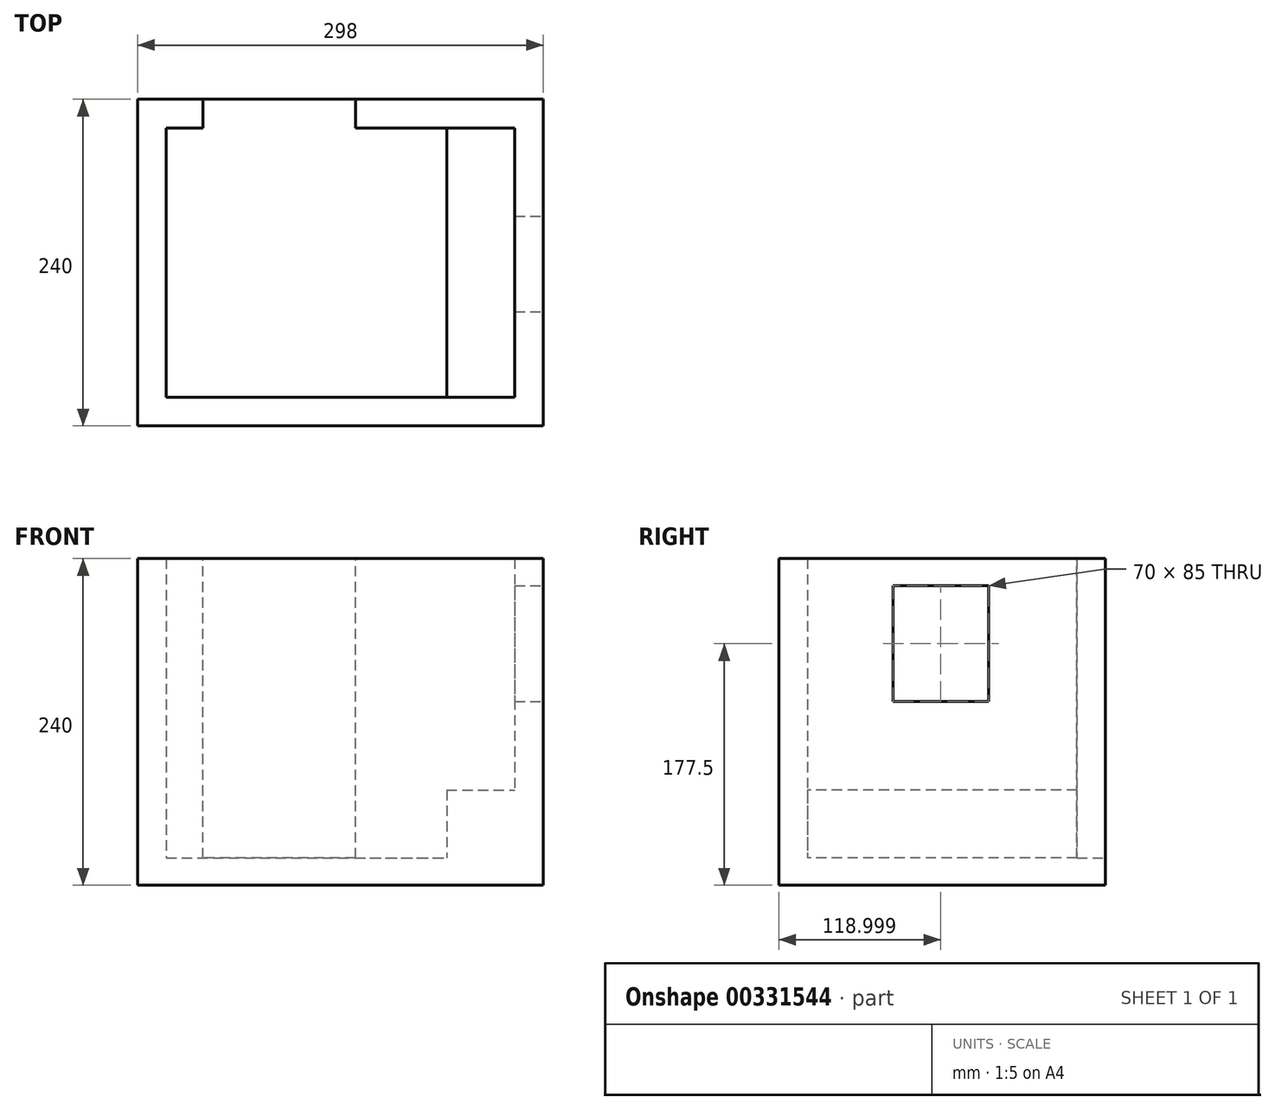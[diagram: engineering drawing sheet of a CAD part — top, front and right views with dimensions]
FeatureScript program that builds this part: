
annotation { "Feature Type Name" : "Feature", "Feature Type Description" : "" }
export const myFeature = defineFeature(function(context is Context, id is Id, definition is map)
    precondition{}
    {
        {
            var Q0;
            Q0=qCreatedBy(makeId("Top.planeOp"),FACE);
            var sketch = newSketch(context, id + "F0", { "sketchPlane" : qUnion([Q0])});
            skLineSegment(sketch, "E0", {"start": v(1313, 440) * mm, "end": v(1313, 406) * mm});
            skLineSegment(sketch, "E1", {"start": v(1313, -267) * mm, "end": v(1313, -301) * mm});
            skLineSegment(sketch, "E2", {"start": v(1313, -301) * mm, "end": v(647, -301) * mm});
            skLineSegment(sketch, "E3", {"start": v(1279, -267) * mm, "end": v(647, -267) * mm});
            skLineSegment(sketch, "E4", {"start": v(1279, 406) * mm, "end": v(688, 406) * mm});
            skLineSegment(sketch, "E5", {"start": v(688, 406) * mm, "end": v(688, -75) * mm});
            skLineSegment(sketch, "E6", {"start": v(688, -75) * mm, "end": v(413, -75) * mm});
            skLineSegment(sketch, "E7", {"start": v(647, -301) * mm, "end": v(647, -267) * mm});
            skLineSegment(sketch, "E8", {"start": v(536, -301) * mm, "end": v(536, -267) * mm});
            skLineSegment(sketch, "E9", {"start": v(536, -267) * mm, "end": v(328, -267) * mm});
            skLineSegment(sketch, "E10", {"start": v(328, -267) * mm, "end": v(328, -407) * mm});
            skLineSegment(sketch, "E11", {"start": v(328, -407) * mm, "end": v(-40, -407) * mm});
            skLineSegment(sketch, "E12", {"start": v(-40, -407) * mm, "end": v(-40, -188) * mm});
            skLineSegment(sketch, "E13", {"start": v(-40, -188) * mm, "end": v(-105, -188) * mm});
            skLineSegment(sketch, "E14", {"start": v(536, -301) * mm, "end": v(362, -301) * mm});
            skLineSegment(sketch, "E15", {"start": v(362, -301) * mm, "end": v(362, -440) * mm});
            skLineSegment(sketch, "E16", {"start": v(-60, -407) * mm, "end": v(-60, -215) * mm});
            skLineSegment(sketch, "E17", {"start": v(-60, -215) * mm, "end": v(-105, -215) * mm});
            skLineSegment(sketch, "E18", {"start": v(-105, -188) * mm, "end": v(-105, -215) * mm});
            skLineSegment(sketch, "E19", {"start": v(-60, -407) * mm, "end": v(-282, -407) * mm});
            skLineSegment(sketch, "E20", {"start": v(-282, -407) * mm, "end": v(-282, -287) * mm});
            skLineSegment(sketch, "E21", {"start": v(-282, -287) * mm, "end": v(-330, -287) * mm});
            skLineSegment(sketch, "E22", {"start": v(-330, -287) * mm, "end": v(-330, -407) * mm});
            skLineSegment(sketch, "E23", {"start": v(-330, -407) * mm, "end": v(-497, -407) * mm});
            skLineSegment(sketch, "E24", {"start": v(-197, -188) * mm, "end": v(-197, -215) * mm});
            skLineSegment(sketch, "E25", {"start": v(-197, -188) * mm, "end": v(-765, -188) * mm});
            skLineSegment(sketch, "E26", {"start": v(-197, -215) * mm, "end": v(-497, -215) * mm});
            skLineSegment(sketch, "E27", {"start": v(-497, -215) * mm, "end": v(-497, -231) * mm});
            skLineSegment(sketch, "E28", {"start": v(-497, -231) * mm, "end": v(-497, -293) * mm});
            skLineSegment(sketch, "E29", {"start": v(-497, -407) * mm, "end": v(-497, -349) * mm});
            skLineSegment(sketch, "E30", {"start": v(413, -75) * mm, "end": v(413, -54) * mm});
            skLineSegment(sketch, "E31", {"start": v(413, -54) * mm, "end": v(667, -54) * mm});
            skLineSegment(sketch, "E32", {"start": v(667, -54) * mm, "end": v(667, 406) * mm});
            skLineSegment(sketch, "E33", {"start": v(667, 406) * mm, "end": v(495, 406) * mm});
            skLineSegment(sketch, "E34", {"start": v(312, 406) * mm, "end": v(391, 406) * mm});
            skLineSegment(sketch, "E35", {"start": v(391, 406) * mm, "end": v(391, 440) * mm});
            skLineSegment(sketch, "E36", {"start": v(495, 406) * mm, "end": v(495, 440) * mm});
            skLineSegment(sketch, "E37", {"start": v(1313, 440) * mm, "end": v(495, 440) * mm});
            skLineSegment(sketch, "E38", {"start": v(312, -75) * mm, "end": v(60, -75) * mm});
            skLineSegment(sketch, "E39", {"start": v(-1279, 406) * mm, "end": v(-1279, 7) * mm});
            skLineSegment(sketch, "E40", {"start": v(-790, 406) * mm, "end": v(-790, 7) * mm});
            skLineSegment(sketch, "E41", {"start": v(-1279, 7) * mm, "end": v(-910, 7) * mm});
            skLineSegment(sketch, "E42", {"start": v(-790, 7) * mm, "end": v(-808, 7) * mm});
            skLineSegment(sketch, "E43", {"start": v(-765, -188) * mm, "end": v(-765, -208) * mm});
            skLineSegment(sketch, "E44", {"start": v(290, 141) * mm, "end": v(290, 406) * mm});
            skLineSegment(sketch, "E45", {"start": v(290, 141) * mm, "end": v(75, 141) * mm});
            skLineSegment(sketch, "E46", {"start": v(75, -46) * mm, "end": v(75, 141) * mm});
            skLineSegment(sketch, "E47", {"start": v(60, -75) * mm, "end": v(60, -46) * mm});
            skLineSegment(sketch, "E48", {"start": v(391, 406) * mm, "end": v(312, 406) * mm});
            skLineSegment(sketch, "E49", {"start": v(-139, 406) * mm, "end": v(-139, 440) * mm});
            skLineSegment(sketch, "E50", {"start": v(-318, 406) * mm, "end": v(-318, 440) * mm});
            skLineSegment(sketch, "E51", {"start": v(-515, 406) * mm, "end": v(-515, 440) * mm});
            skLineSegment(sketch, "E52", {"start": v(-694, 406) * mm, "end": v(-694, 440) * mm});
            skLineSegment(sketch, "E53", {"start": v(-770, 406) * mm, "end": v(-770, 9) * mm});
            skLineSegment(sketch, "E54", {"start": v(-694, 406) * mm, "end": v(-770, 406) * mm});
            skLineSegment(sketch, "E55", {"start": v(75, 406) * mm, "end": v(-139, 406) * mm});
            skLineSegment(sketch, "E56", {"start": v(-318, 406) * mm, "end": v(-515, 406) * mm});
            skLineSegment(sketch, "E57", {"start": v(-318, 440) * mm, "end": v(-515, 440) * mm});
            skLineSegment(sketch, "E58", {"start": v(-770, 9) * mm, "end": v(-754, 9) * mm});
            skLineSegment(sketch, "E59", {"start": v(-677, 9) * mm, "end": v(-659, 9) * mm});
            skLineSegment(sketch, "E60", {"start": v(-659, 9) * mm, "end": v(-659, -5) * mm});
            skLineSegment(sketch, "E61", {"start": v(-659, -5) * mm, "end": v(-659, -46) * mm});
            skLineSegment(sketch, "E62", {"start": v(-659, -46) * mm, "end": v(-60, -46) * mm});
            skLineSegment(sketch, "E63", {"start": v(-60, -75) * mm, "end": v(-60, -46) * mm});
            skLineSegment(sketch, "E64", {"start": v(60, -75) * mm, "end": v(128, -75) * mm});
            skLineSegment(sketch, "E65", {"start": v(60, -46) * mm, "end": v(75, -46) * mm});
            skLineSegment(sketch, "E66", {"start": v(96, -46) * mm, "end": v(290, -46) * mm});
            skLineSegment(sketch, "E67", {"start": v(-60, -75) * mm, "end": v(-677, -75) * mm});
            skLineSegment(sketch, "E68", {"start": v(-677, 9) * mm, "end": v(-677, -75) * mm});
            skLineSegment(sketch, "E69", {"start": v(-754, 9) * mm, "end": v(-754, -13) * mm});
            skLineSegment(sketch, "E70", {"start": v(-808, 7) * mm, "end": v(-808, -13) * mm});
            skLineSegment(sketch, "E71", {"start": v(-808, -13) * mm, "end": v(-754, -13) * mm});
            skLineSegment(sketch, "E72", {"start": v(-910, 7) * mm, "end": v(-910, -29) * mm});
            skLineSegment(sketch, "E73", {"start": v(-1279, -406) * mm, "end": v(-935, -406) * mm});
            skLineSegment(sketch, "E74", {"start": v(-1313, -440) * mm, "end": v(-935, -440) * mm});
            skLineSegment(sketch, "E75", {"start": v(-910, -29) * mm, "end": v(-935, -29) * mm});
            skLineSegment(sketch, "E76", {"start": v(-935, -13) * mm, "end": v(-1279, -13) * mm});
            skLineSegment(sketch, "E77", {"start": v(-910, -132) * mm, "end": v(-935, -132) * mm});
            skLineSegment(sketch, "E78", {"start": v(-910, -29) * mm, "end": v(-910, -13) * mm});
            skLineSegment(sketch, "E79", {"start": v(-935, -406) * mm, "end": v(-935, -132) * mm});
            skLineSegment(sketch, "E80", {"start": v(-935, -29) * mm, "end": v(-935, -13) * mm});
            skLineSegment(sketch, "E81", {"start": v(-877, -208) * mm, "end": v(-877, -188) * mm});
            skLineSegment(sketch, "E82", {"start": v(-910, -132) * mm, "end": v(-910, -188) * mm});
            skLineSegment(sketch, "E83", {"start": v(-877, -188) * mm, "end": v(-910, -188) * mm});
            skLineSegment(sketch, "E84", {"start": v(-877, -208) * mm, "end": v(-904, -208) * mm});
            skLineSegment(sketch, "E85", {"start": v(-904, -208) * mm, "end": v(-904, -406) * mm});
            skLineSegment(sketch, "E86", {"start": v(-904, -406) * mm, "end": v(-648, -406) * mm});
            skLineSegment(sketch, "E87", {"start": v(-765, -208) * mm, "end": v(-648, -208) * mm});
            skLineSegment(sketch, "E88", {"start": v(-648, -208) * mm, "end": v(-648, -273) * mm});
            skLineSegment(sketch, "E89", {"start": v(-648, -406) * mm, "end": v(-648, -343) * mm});
            skLineSegment(sketch, "E90", {"start": v(-935, -440) * mm, "end": v(362, -440) * mm});
            skLineSegment(sketch, "E91", {"start": v(151, 406) * mm, "end": v(151, 440) * mm});
            skLineSegment(sketch, "E92", {"start": v(224, 406) * mm, "end": v(224, 440) * mm});
            skLineSegment(sketch, "E93", {"start": v(290, 406) * mm, "end": v(224, 406) * mm});
            skLineSegment(sketch, "E94", {"start": v(151, 406) * mm, "end": v(96, 406) * mm});
            skLineSegment(sketch, "E95", {"start": v(391, 440) * mm, "end": v(224, 440) * mm});
            skLineSegment(sketch, "E96", {"start": v(151, 440) * mm, "end": v(-139, 440) * mm});
            skLineSegment(sketch, "E97", {"start": v(-907, 406) * mm, "end": v(-907, 440) * mm});
            skLineSegment(sketch, "E98", {"start": v(-1085, 406) * mm, "end": v(-1085, 440) * mm});
            skLineSegment(sketch, "E99", {"start": v(-790, 406) * mm, "end": v(-907, 406) * mm});
            skLineSegment(sketch, "E100", {"start": v(-1085, 406) * mm, "end": v(-1279, 406) * mm});
            skLineSegment(sketch, "E101", {"start": v(-694, 440) * mm, "end": v(-907, 440) * mm});
            skLineSegment(sketch, "E102", {"start": v(-1085, 440) * mm, "end": v(-1313, 440) * mm});
            skLineSegment(sketch, "E103", {"start": v(-1279, -118) * mm, "end": v(-1313, -118) * mm});
            skLineSegment(sketch, "E104", {"start": v(-1279, -297) * mm, "end": v(-1313, -297) * mm});
            skLineSegment(sketch, "E105", {"start": v(-1279, -13) * mm, "end": v(-1279, -118) * mm});
            skLineSegment(sketch, "E106", {"start": v(-1279, -297) * mm, "end": v(-1279, -406) * mm});
            skLineSegment(sketch, "E107", {"start": v(-1313, 440) * mm, "end": v(-1313, -118) * mm});
            skLineSegment(sketch, "E108", {"start": v(-1313, -297) * mm, "end": v(-1313, -440) * mm});
            skLineSegment(sketch, "E109", {"start": v(-648, -273) * mm, "end": v(-630, -273) * mm});
            skLineSegment(sketch, "E110", {"start": v(-648, -343) * mm, "end": v(-630, -343) * mm});
            skLineSegment(sketch, "E111", {"start": v(-515, -349) * mm, "end": v(-497, -349) * mm});
            skLineSegment(sketch, "E112", {"start": v(-515, -293) * mm, "end": v(-497, -293) * mm});
            skLineSegment(sketch, "E113", {"start": v(-515, -349) * mm, "end": v(-515, -406) * mm});
            skLineSegment(sketch, "E114", {"start": v(-630, -343) * mm, "end": v(-630, -406) * mm});
            skLineSegment(sketch, "E115", {"start": v(-630, -406) * mm, "end": v(-515, -406) * mm});
            skLineSegment(sketch, "E116", {"start": v(-630, -273) * mm, "end": v(-630, -206) * mm});
            skLineSegment(sketch, "E117", {"start": v(-630, -206) * mm, "end": v(-515, -206) * mm});
            skLineSegment(sketch, "E118", {"start": v(-515, -293) * mm, "end": v(-515, -206) * mm});
            skLineSegment(sketch, "E119", {"start": v(290, 43) * mm, "end": v(312, 43) * mm});
            skLineSegment(sketch, "E120", {"start": v(290, 124) * mm, "end": v(312, 124) * mm});
            skLineSegment(sketch, "E121", {"start": v(312, -75) * mm, "end": v(312, 43) * mm});
            skLineSegment(sketch, "E122", {"start": v(312, 124) * mm, "end": v(312, 406) * mm});
            skLineSegment(sketch, "E123", {"start": v(290, -46) * mm, "end": v(290, 43) * mm});
            skLineSegment(sketch, "E124", {"start": v(96, 222) * mm, "end": v(75, 222) * mm});
            skLineSegment(sketch, "E125", {"start": v(96, 222) * mm, "end": v(96, 406) * mm});
            skLineSegment(sketch, "E126", {"start": v(75, 222) * mm, "end": v(75, 406) * mm});
            skLineSegment(sketch, "E127", {"start": v(96, -46) * mm, "end": v(96, 124) * mm});
            skLineSegment(sketch, "E128", {"start": v(290, 124) * mm, "end": v(96, 124) * mm});
            skLineSegment(sketch, "E129", {"start": v(1279, -219) * mm, "end": v(1313, -219) * mm});
            skLineSegment(sketch, "E130", {"start": v(1279, -26) * mm, "end": v(1313, -26) * mm});
            skLineSegment(sketch, "E131", {"start": v(1279, 46) * mm, "end": v(1313, 46) * mm});
            skLineSegment(sketch, "E132", {"start": v(1279, 239) * mm, "end": v(1313, 239) * mm});
            skLineSegment(sketch, "E133", {"start": v(1313, 406) * mm, "end": v(1313, 239) * mm});
            skLineSegment(sketch, "E134", {"start": v(1279, 406) * mm, "end": v(1279, 239) * mm});
            skLineSegment(sketch, "E135", {"start": v(1313, 46) * mm, "end": v(1313, -26) * mm});
            skLineSegment(sketch, "E136", {"start": v(1313, -219) * mm, "end": v(1313, -267) * mm});
            skLineSegment(sketch, "E137", {"start": v(1279, 46) * mm, "end": v(1279, -26) * mm});
            skLineSegment(sketch, "E138", {"start": v(1279, -219) * mm, "end": v(1279, -267) * mm});
            skLineSegment(sketch, "E139", {"start": v(1313, -301) * mm, "end": v(1313, 440) * mm});
            skLineSegment(sketch, "E140", {"start": v(1313, -301) * mm, "end": v(362, -301) * mm});
            skLineSegment(sketch, "E141", {"start": v(362, -440) * mm, "end": v(-1313, -440) * mm});
            skLineSegment(sketch, "E142", {"start": v(-1313, 440) * mm, "end": v(-1313, -440) * mm});
            skLineSegment(sketch, "E143", {"start": v(-1313, 440) * mm, "end": v(1313, 440) * mm});
            skLineSegment(sketch, "E144", {"start": v(-321.5, -37.21) * mm, "end": v(-321.5, 162.79) * mm});
            skLineSegment(sketch, "E145", {"start": v(-321.5, -37.21) * mm, "end": v(-511.5, -37.21) * mm});
            skLineSegment(sketch, "E146", {"start": v(-321.5, 162.79) * mm, "end": v(-511.5, 162.79) * mm});
            skLineSegment(sketch, "E147", {"start": v(-511.5, -37.21) * mm, "end": v(-511.5, 162.79) * mm});
            skLineSegment(sketch, "E148", {"start": v(-321.5, -29.2) * mm, "end": v(-511.5, -29.2) * mm});
            skLineSegment(sketch, "E149", {"start": v(-499.08, -21.75) * mm, "end": v(-430.85, -21.75) * mm});
            skLineSegment(sketch, "E150", {"start": v(-430.85, -21.75) * mm, "end": v(-430.85, 2.94) * mm});
            skLineSegment(sketch, "E151", {"start": v(-430.85, 2.94) * mm, "end": v(-499.08, 2.94) * mm});
            skLineSegment(sketch, "E152", {"start": v(-499.08, 2.94) * mm, "end": v(-499.08, -21.75) * mm});
            skLineSegment(sketch, "E153", {"start": v(-333.92, -21.75) * mm, "end": v(-402.15, -21.75) * mm});
            skLineSegment(sketch, "E154", {"start": v(-402.15, -21.75) * mm, "end": v(-402.15, 2.94) * mm});
            skLineSegment(sketch, "E155", {"start": v(-402.15, 2.94) * mm, "end": v(-333.92, 2.94) * mm});
            skLineSegment(sketch, "E156", {"start": v(-333.92, 2.94) * mm, "end": v(-333.92, -21.75) * mm});
            skLineSegment(sketch, "E157", {"start": v(-321.5, 13.1) * mm, "end": v(-416.5, 13.1) * mm});
            skLineSegment(sketch, "E158", {"start": v(-511.5, 36.6) * mm, "end": v(-491.94, 63.04) * mm});
            skLineSegment(sketch, "E159", {"start": v(-491.94, 63.04) * mm, "end": v(-416.5, 13.1) * mm});
            skLineSegment(sketch, "E160", {"start": v(-416.5, 13.1) * mm, "end": v(-511.5, 36.6) * mm});
            skLineSegment(sketch, "E161", {"start": v(-321.5, 159.23) * mm, "end": v(-511.5, 159.23) * mm});
            skLineSegment(sketch, "E162", {"start": v(-552.43, 3.31) * mm, "end": v(-520.43, 3.31) * mm});
            skLineSegment(sketch, "E163", {"start": v(-552.43, 3.31) * mm, "end": v(-552.43, -36.7) * mm});
            skLineSegment(sketch, "E164", {"start": v(-520.43, 3.31) * mm, "end": v(-520.43, -36.7) * mm});
            skLineSegment(sketch, "E165", {"start": v(-552.43, -36.7) * mm, "end": v(-520.43, -36.7) * mm});
            skLineSegment(sketch, "E166", {"start": v(-552.43, -6.69) * mm, "end": v(-520.43, -6.69) * mm});
            skLineSegment(sketch, "E167", {"start": v(-552.43, -3.69) * mm, "end": v(-520.43, -3.69) * mm});
            skLineSegment(sketch, "E168", {"start": v(-552.43, -0.69) * mm, "end": v(-520.43, -0.69) * mm});
            skLineSegment(sketch, "E169", {"start": v(-552.43, 2.31) * mm, "end": v(-520.43, 2.31) * mm});
            skLineSegment(sketch, "E170", {"start": v(-280.57, 3.31) * mm, "end": v(-312.57, 3.31) * mm});
            skLineSegment(sketch, "E171", {"start": v(-280.57, 3.31) * mm, "end": v(-280.57, -36.7) * mm});
            skLineSegment(sketch, "E172", {"start": v(-312.57, 3.31) * mm, "end": v(-312.57, -36.7) * mm});
            skLineSegment(sketch, "E173", {"start": v(-280.57, -36.7) * mm, "end": v(-312.57, -36.7) * mm});
            skLineSegment(sketch, "E174", {"start": v(-280.57, -6.69) * mm, "end": v(-312.57, -6.69) * mm});
            skLineSegment(sketch, "E175", {"start": v(-280.57, -3.69) * mm, "end": v(-312.57, -3.69) * mm});
            skLineSegment(sketch, "E176", {"start": v(-280.57, -0.69) * mm, "end": v(-312.57, -0.69) * mm});
            skLineSegment(sketch, "E177", {"start": v(-280.57, 2.31) * mm, "end": v(-312.57, 2.31) * mm});
            skLineSegment(sketch, "E178", {"start": v(-765, 395.6) * mm, "end": v(-765, 20.6) * mm});
            skLineSegment(sketch, "E179", {"start": v(-765, 395.6) * mm, "end": v(-705, 395.6) * mm});
            skLineSegment(sketch, "E180", {"start": v(-705, 395.6) * mm, "end": v(-705, 20.6) * mm});
            skLineSegment(sketch, "E181", {"start": v(-765, 20.6) * mm, "end": v(-705, 20.6) * mm});
            skLineSegment(sketch, "E182", {"start": v(-705, 395.6) * mm, "end": v(-700, 395.6) * mm});
            skLineSegment(sketch, "E183", {"start": v(-700, 395.6) * mm, "end": v(-700, 20.6) * mm});
            skLineSegment(sketch, "E184", {"start": v(-705, 20.6) * mm, "end": v(-700, 20.6) * mm});
            skLineSegment(sketch, "E185", {"start": v(-705, 114.35) * mm, "end": v(-700, 114.35) * mm});
            skLineSegment(sketch, "E186", {"start": v(-705, 301.85) * mm, "end": v(-700, 301.85) * mm});
            skLineSegment(sketch, "E187", {"start": v(-705, 208.1) * mm, "end": v(-700, 208.1) * mm});
            skLineSegment(sketch, "E188", {"start": v(-705, 348.73) * mm, "end": v(-700, 348.73) * mm});
            skLineSegment(sketch, "E189", {"start": v(-705, 67.47) * mm, "end": v(-700, 67.47) * mm});
            skSolve(sketch);
        }
        {
            var Q0;
            Q0=makeQuery(id+"F0.imprint","IMPRINT",FACE,{"disambiguationData":[TD([[makeQuery(id+"F0.imprint","IMPRINT",EDGE,{"derivedFrom":sQuery(id+"F0.wireOp",EDGE,"E3")}),-1.0]])]});
            var sketch = newSketch(context, id + "F1", { "sketchPlane" : qUnion([Q0])});
            skLineSegment(sketch, "E190.0", {"start": v(-904, -208) * mm, "end": v(-904, -406) * mm});
            skLineSegment(sketch, "E191.0", {"start": v(-904, -406) * mm, "end": v(-648, -406) * mm});
            skLineSegment(sketch, "E192.0", {"start": v(-648, -208) * mm, "end": v(-648, -273) * mm});
            skLineSegment(sketch, "E193.0", {"start": v(-648, -406) * mm, "end": v(-648, -343) * mm});
            skLineSegment(sketch, "E194.0", {"start": v(-765, -208) * mm, "end": v(-648, -208) * mm});
            skLineSegment(sketch, "E195", {"start": v(-648, -273) * mm, "end": v(-648, -343) * mm});
            skLineSegment(sketch, "E196", {"start": v(-765, -208) * mm, "end": v(-904, -208) * mm});
            skSolve(sketch);
        }
        {
            var Q0;
            {var subQ0=sQuery(id+"F1.wireOp",EDGE,"E190.0");Q0=makeQuery(id+"F1.imprint","IMPRINT",FACE,{"disambiguationData":[TD([[makeQuery(id+"F1.imprint","IMPRINT",EDGE,{"derivedFrom":subQ0}),1.0]])]});}
            var sketch = newSketch(context, id + "F2", { "sketchPlane" : qUnion([Q0])});
            skLineSegment(sketch, "E197.0", {"start": v(-627, -273) * mm, "end": v(-627, -187) * mm});
            skLineSegment(sketch, "E197.1", {"start": v(-627, -343) * mm, "end": v(-627, -273) * mm});
            skLineSegment(sketch, "E197.2", {"start": v(-627, -187) * mm, "end": v(-765, -187) * mm});
            skLineSegment(sketch, "E197.3", {"start": v(-627, -427) * mm, "end": v(-627, -343) * mm});
            skLineSegment(sketch, "E197.4", {"start": v(-765, -187) * mm, "end": v(-877, -187) * mm});
            skLineSegment(sketch, "E197.5", {"start": v(-877, -187) * mm, "end": v(-925, -187) * mm});
            skLineSegment(sketch, "E197.6", {"start": v(-925, -187) * mm, "end": v(-925, -427) * mm});
            skLineSegment(sketch, "E197.7", {"start": v(-925, -427) * mm, "end": v(-627, -427) * mm});
            skLineSegment(sketch, "E198.0.0", {"start": v(-648, -208) * mm, "end": v(-765, -208) * mm});
            skLineSegment(sketch, "E198.0.1", {"start": v(-765, -208) * mm, "end": v(-877, -208) * mm});
            skLineSegment(sketch, "E198.0.2", {"start": v(-877, -208) * mm, "end": v(-904, -208) * mm});
            skLineSegment(sketch, "E198.0.3", {"start": v(-904, -208) * mm, "end": v(-904, -406) * mm});
            skLineSegment(sketch, "E198.0.4", {"start": v(-904, -406) * mm, "end": v(-648, -406) * mm});
            skLineSegment(sketch, "E198.0.5", {"start": v(-648, -406) * mm, "end": v(-648, -343) * mm});
            skLineSegment(sketch, "E198.0.6", {"start": v(-648, -343) * mm, "end": v(-648, -273) * mm});
            skLineSegment(sketch, "E198.0.7", {"start": v(-648, -273) * mm, "end": v(-648, -208) * mm});
            skSolve(sketch);
        }
        {
            var Q0;
            Q0 = qSketchRegion(id + "F2", true);
            extrude(context, id + "F3", {"entities" : qUnion([Q0]), "depth" : (220 + 20) * mm});
        }
        {
            var Q0;
            {var subQ0=sQuery(id+"F1.wireOp",EDGE,"E190.0");Q0=makeQuery(id+"F1.imprint","IMPRINT",FACE,{"disambiguationData":[TD([[makeQuery(id+"F1.imprint","IMPRINT",EDGE,{"derivedFrom":subQ0}),1.0]])]});}
            var sketch = newSketch(context, id + "F4", { "sketchPlane" : qUnion([Q0])});
            skLineSegment(sketch, "E199.0.0", {"start": v(-648, -208) * mm, "end": v(-765, -208) * mm});
            skLineSegment(sketch, "E199.0.1", {"start": v(-765, -208) * mm, "end": v(-877, -208) * mm});
            skLineSegment(sketch, "E199.0.2", {"start": v(-877, -208) * mm, "end": v(-904, -208) * mm});
            skLineSegment(sketch, "E199.0.3", {"start": v(-904, -208) * mm, "end": v(-904, -406) * mm});
            skLineSegment(sketch, "E199.0.4", {"start": v(-904, -406) * mm, "end": v(-648, -406) * mm});
            skLineSegment(sketch, "E199.0.5", {"start": v(-648, -406) * mm, "end": v(-648, -343) * mm});
            skLineSegment(sketch, "E199.0.6", {"start": v(-648, -343) * mm, "end": v(-648, -273) * mm});
            skLineSegment(sketch, "E199.0.7", {"start": v(-648, -273) * mm, "end": v(-648, -208) * mm});
            skSolve(sketch);
        }
        {
            var Q0;
            Q0 = qSketchRegion(id + "F4", true);
            extrude(context, id + "F5", {"entities" : qUnion([Q0]), "operationType" : NewBodyOperationType.ADD, "depth" : 20 * mm});
        }
        {
            var Q0;
            Q0=makeQuery(id+"F3.opExtrude","SWEPT_FACE",FACE,{"disambiguationData":[OSD([sQuery(id+"F2.wireOp",EDGE,"E197.2"),sQuery(id+"F2.wireOp",EDGE,"E197.4"),sQuery(id+"F2.wireOp",EDGE,"E197.5")])]});
            var sketch = newSketch(context, id + "F6", { "sketchPlane" : qUnion([Q0])});
            skLineSegment(sketch, "E200.0", {"start": v(904, 240) * mm, "end": v(904, 20) * mm});
            skLineSegment(sketch, "E201.0", {"start": v(877, 0) * mm, "end": v(910, 0) * mm});
            skLineSegment(sketch, "E202.0", {"start": v(197, 0) * mm, "end": v(765, 0) * mm});
            skLineSegment(sketch, "E203", {"start": v(877, 20) * mm, "end": v(877, 261.1) * mm});
            skLineSegment(sketch, "E204", {"start": v(877, 261.1) * mm, "end": v(765, 261.1) * mm});
            skLineSegment(sketch, "E205", {"start": v(765, 261.1) * mm, "end": v(765, 20) * mm});
            skLineSegment(sketch, "E206", {"start": v(765, 20) * mm, "end": v(877, 20) * mm});
            skSolve(sketch);
        }
        {
            var Q0;
            Q0 = qSketchRegion(id + "F6", true);
            extrude(context, id + "F7", {"entities" : qUnion([Q0]), "operationType" : NewBodyOperationType.REMOVE, "oppositeDirection" : true, "depth" : 25 * mm});
        }
        {
            var Q0;
            Q0=makeQuery(id+"F3.opExtrude","SWEPT_FACE",FACE,{"disambiguationData":[OSD([sQuery(id+"F2.wireOp",EDGE,"E197.0"),sQuery(id+"F2.wireOp",EDGE,"E197.1"),sQuery(id+"F2.wireOp",EDGE,"E197.3")])]});
            var sketch = newSketch(context, id + "F8", { "sketchPlane" : qUnion([Q0])});
            skLineSegment(sketch, "E207.0", {"start": v(-208, 0) * mm, "end": v(-273, 0) * mm, "construction": true});
            skLineSegment(sketch, "E208.0", {"start": v(-406, 0) * mm, "end": v(-343, 0) * mm, "construction": true});
            skLineSegment(sketch, "E209.0", {"start": v(-406, 20) * mm, "end": v(-208, 20) * mm, "construction": true});
            skLineSegment(sketch, "E210", {"start": v(-273, 135) * mm, "end": v(-343, 135) * mm});
            skLineSegment(sketch, "E211", {"start": v(-343, 135) * mm, "end": v(-343, 220) * mm});
            skLineSegment(sketch, "E212", {"start": v(-343, 220) * mm, "end": v(-273, 220) * mm});
            skLineSegment(sketch, "E213", {"start": v(-273, 220) * mm, "end": v(-273, 135) * mm});
            skSolve(sketch);
        }
        {
            var Q0;
            Q0 = qSketchRegion(id + "F8", true);
            extrude(context, id + "F9", {"entities" : qUnion([Q0]), "operationType" : NewBodyOperationType.REMOVE, "oppositeDirection" : true, "depth" : 25 * mm});
        }
        {
            var Q0;
            Q0=makeQuery(id+"F7.boolean.opBoolean","MERGE",FACE,{"derivedFrom":[makeQuery(id+"F5.opExtrude","CAP_FACE",FACE,{"disambiguationData":[OSD([sQuery(id+"F4.wireOp",EDGE,"E199.0.0"),sQuery(id+"F4.wireOp",EDGE,"E199.0.1"),sQuery(id+"F4.wireOp",EDGE,"E199.0.2"),sQuery(id+"F4.wireOp",EDGE,"E199.0.3"),sQuery(id+"F4.wireOp",EDGE,"E199.0.4"),sQuery(id+"F4.wireOp",EDGE,"E199.0.5"),sQuery(id+"F4.wireOp",EDGE,"E199.0.6"),sQuery(id+"F4.wireOp",EDGE,"E199.0.7")])],"isStart":false}),makeQuery(id+"F7.opExtrude","SWEPT_FACE",FACE,{"disambiguationData":[OSD([sQuery(id+"F6.wireOp",EDGE,"E206")])]})]});
            var sketch = newSketch(context, id + "F10", { "sketchPlane" : qUnion([Q0])});
            skLineSegment(sketch, "E214.0", {"start": v(-648, -406) * mm, "end": v(-648, -208) * mm});
            skLineSegment(sketch, "E215", {"start": v(-648, -208) * mm, "end": v(-698, -208) * mm});
            skLineSegment(sketch, "E216", {"start": v(-698, -208) * mm, "end": v(-698, -406) * mm});
            skLineSegment(sketch, "E217", {"start": v(-698, -406) * mm, "end": v(-648, -406) * mm});
            skSolve(sketch);
        }
        {
            var Q0;
            Q0 = qSketchRegion(id + "F10", true);
            extrude(context, id + "F11", {"entities" : qUnion([Q0]), "operationType" : NewBodyOperationType.ADD, "depth" : 50 * mm});
        }
    });
